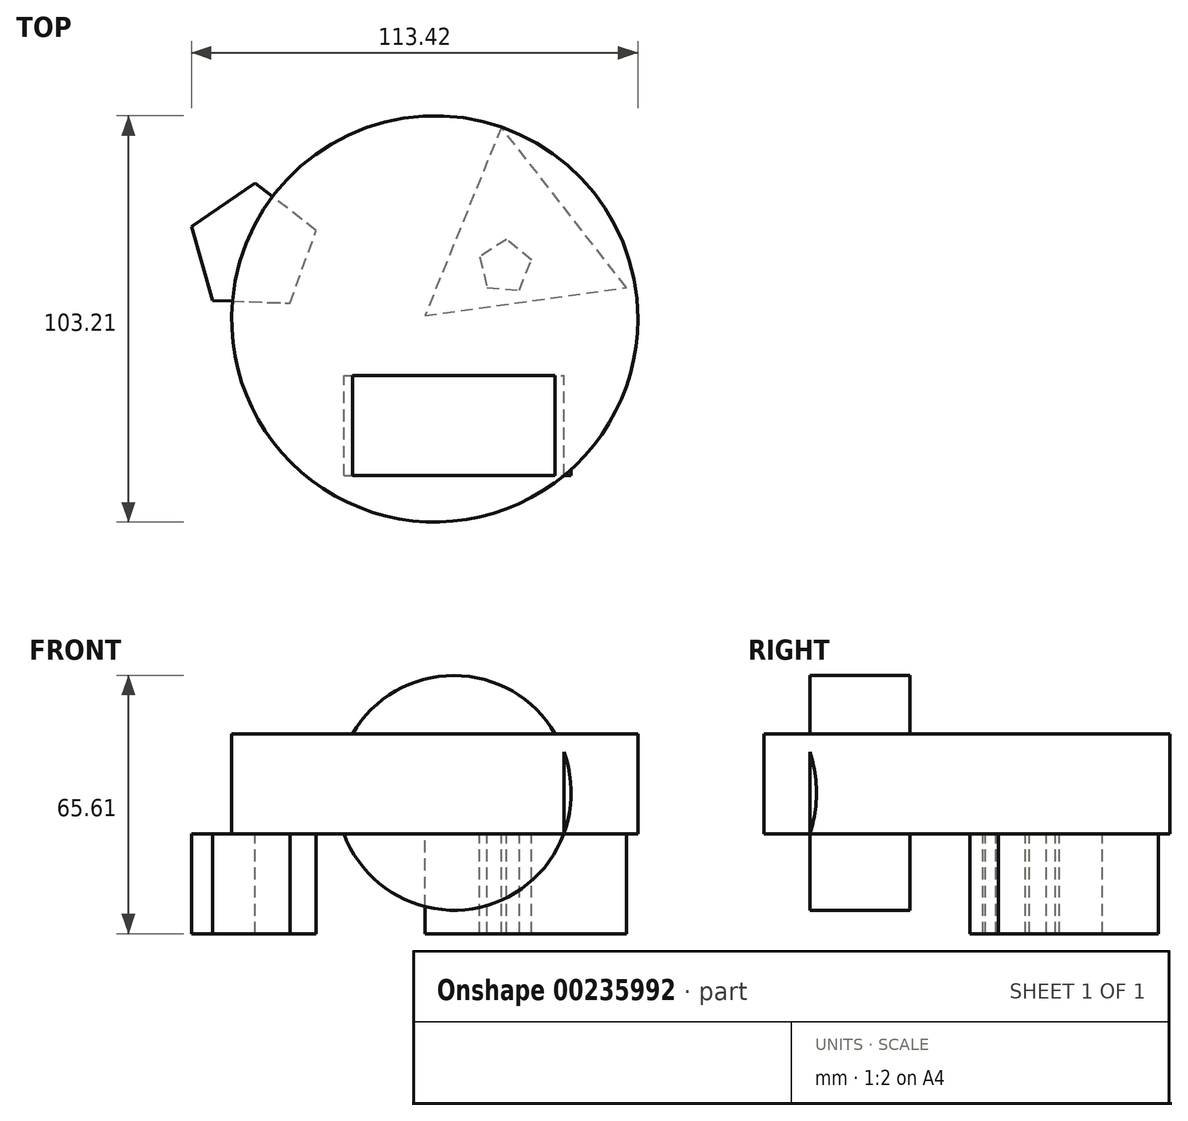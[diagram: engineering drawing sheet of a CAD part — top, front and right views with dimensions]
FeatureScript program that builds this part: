
annotation { "Feature Type Name" : "Feature", "Feature Type Description" : "" }
export const myFeature = defineFeature(function(context is Context, id is Id, definition is map)
    precondition{}
    {
        {
            var Q0;
            Q0=qCreatedBy(makeId("Top.planeOp"),FACE);
            var sketch = newSketch(context, id + "F0", { "sketchPlane" : qUnion([Q0])});
            skCircle(sketch, "E0", {"center": v(-11.87, 14.44) * mm, "radius": 51.6 * mm});
            skSolve(sketch);
        }
        {
            var Q0;
            Q0=makeQuery(id+"F0.imprint","IMPRINT",FACE,{"disambiguationData":[TD([[makeQuery(id+"F0.imprint","IMPRINT",EDGE,{"derivedFrom":sQuery(id+"F0.wireOp",EDGE,"E0")}),1.0]])]});
            extrude(context, id + "F1", {"entities" : qUnion([Q0]), "depth" : 25.4 * mm});
        }
        {
            var Q0;
            Q0=qCreatedBy(makeId("Front.planeOp"),FACE);
            var sketch = newSketch(context, id + "F2", { "sketchPlane" : qUnion([Q0])});
            skCircle(sketch, "E1", {"center": v(-7.02, 10.39) * mm, "radius": 29.82 * mm});
            skSolve(sketch);
        }
        {
            var Q0;
            Q0 = qSketchRegion(id + "F2", true);
            extrude(context, id + "F3", {"entities" : qUnion([Q0]), "operationType" : NewBodyOperationType.ADD, "depth" : 25.4 * mm});
        }
        {
            var Q0;
            Q0=makeQuery(id+"F1.opExtrude","CAP_FACE",FACE,{"disambiguationData":[OSD([sQuery(id+"F0.wireOp",EDGE,"E0")])],"isStart":true});
            var sketch = newSketch(context, id + "F4", { "sketchPlane" : qUnion([Q0])});
            skCircle(sketch, "E2.cCircle", {"center": v(-58.02, -32.25) * mm, "radius": 13.49 * mm, "construction": true});
            skLineSegment(sketch, "E2.0", {"start": v(-48.67, -18.44) * mm, "end": v(-42, -36.87) * mm});
            skLineSegment(sketch, "E2.1", {"start": v(-42, -36.87) * mm, "end": v(-57.47, -48.9) * mm});
            skLineSegment(sketch, "E2.2", {"start": v(-57.47, -48.9) * mm, "end": v(-73.7, -37.92) * mm});
            skLineSegment(sketch, "E2.3", {"start": v(-73.7, -37.92) * mm, "end": v(-68.25, -19.09) * mm});
            skLineSegment(sketch, "E2.4", {"start": v(-68.25, -19.09) * mm, "end": v(-48.67, -18.44) * mm});
            skPoint(sketch, "E2.0.midPoint", {"position": v(-45.33, -27.66) * mm});
            skCircle(sketch, "E3.cCircle", {"center": v(9.17, -33.6) * mm, "radius": 14.91 * mm, "construction": true});
            skLineSegment(sketch, "E3.0", {"start": v(36.82, -22.4) * mm, "end": v(5.04, -63.14) * mm});
            skLineSegment(sketch, "E3.1", {"start": v(5.04, -63.14) * mm, "end": v(-14.34, -15.25) * mm});
            skLineSegment(sketch, "E3.2", {"start": v(-14.34, -15.25) * mm, "end": v(36.82, -22.4) * mm});
            skPoint(sketch, "E3.0.midPoint", {"position": v(20.93, -42.77) * mm});
            skCircle(sketch, "E4.cCircle", {"center": v(5.94, -27.66) * mm, "radius": 5.62 * mm, "construction": true});
            skLineSegment(sketch, "E4.0", {"start": v(9.61, -21.77) * mm, "end": v(12.67, -29.33) * mm});
            skLineSegment(sketch, "E4.1", {"start": v(12.67, -29.33) * mm, "end": v(6.42, -34.58) * mm});
            skLineSegment(sketch, "E4.2", {"start": v(6.42, -34.58) * mm, "end": v(-0.5, -30.26) * mm});
            skLineSegment(sketch, "E4.3", {"start": v(-0.5, -30.26) * mm, "end": v(1.47, -22.34) * mm});
            skLineSegment(sketch, "E4.4", {"start": v(1.47, -22.34) * mm, "end": v(9.61, -21.77) * mm});
            skPoint(sketch, "E4.0.midPoint", {"position": v(11.14, -25.55) * mm});
            skSolve(sketch);
        }
        {
            var Q0;
            Q0 = qSketchRegion(id + "F4", true);
            extrude(context, id + "F5", {"entities" : qUnion([Q0]), "operationType" : NewBodyOperationType.ADD, "depth" : 25.4 * mm});
        }
    });
